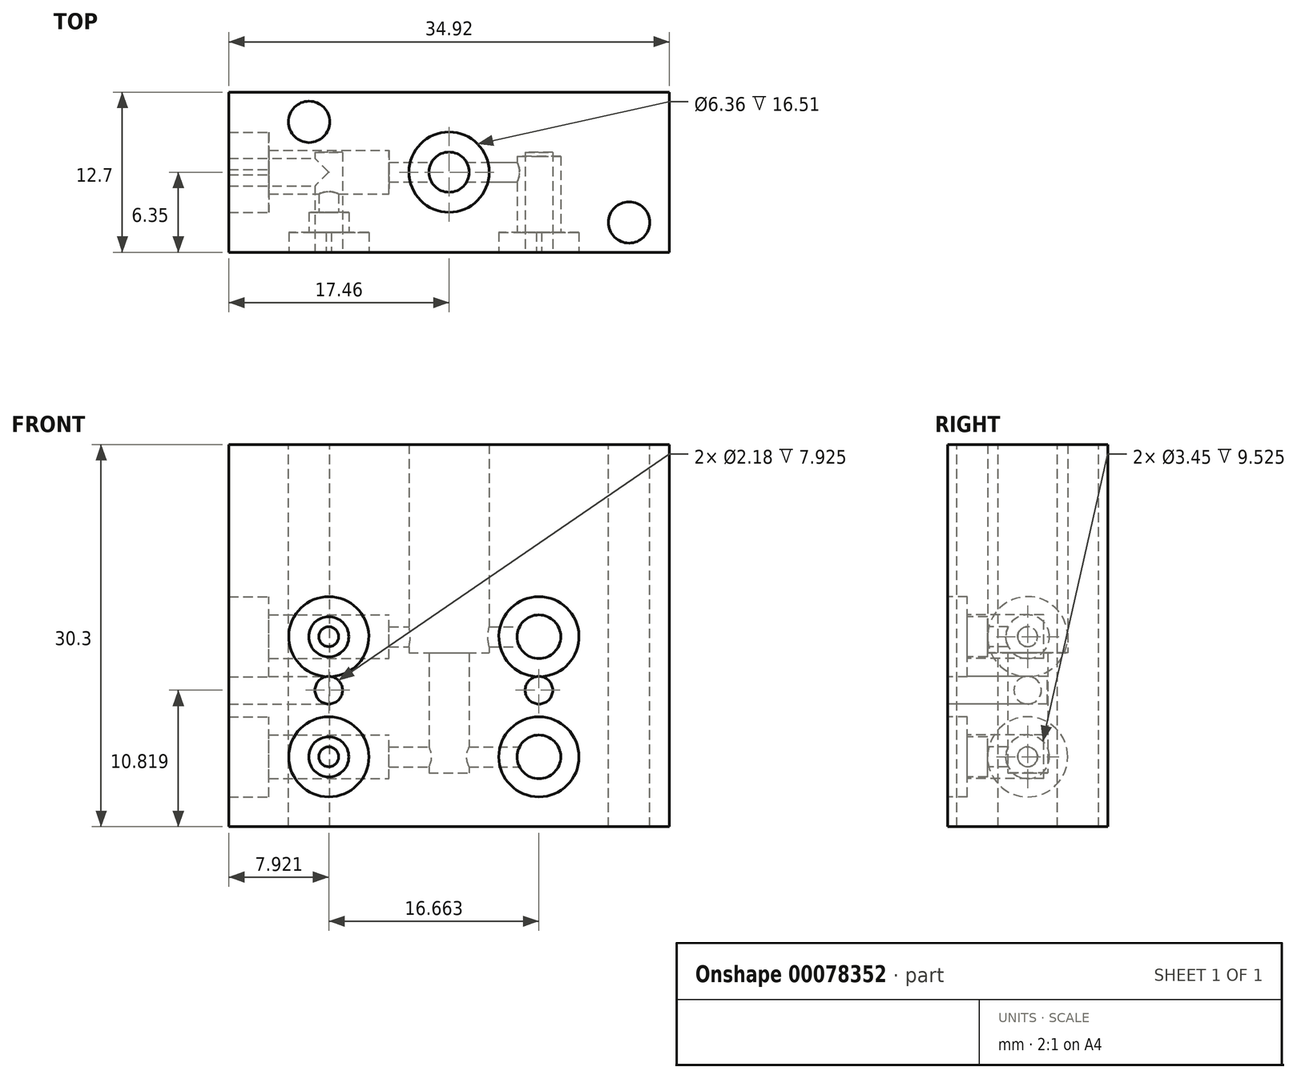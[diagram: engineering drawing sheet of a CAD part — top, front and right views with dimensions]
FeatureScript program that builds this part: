
annotation { "Feature Type Name" : "Feature", "Feature Type Description" : "" }
export const myFeature = defineFeature(function(context is Context, id is Id, definition is map)
    precondition{}
    {
        {
            var Q0;
            Q0=qCreatedBy(makeId("Front.planeOp"),FACE);
            var sketch = newSketch(context, id + "F0", { "sketchPlane" : qUnion([Q0])});
            skLineSegment(sketch, "E0.top", {"start": v(0, 15.15) * mm, "end": v(-17.46, 15.15) * mm});
            skLineSegment(sketch, "E0.right", {"start": v(-17.46, 0) * mm, "end": v(-17.46, 15.15) * mm});
            skLineSegment(sketch, "E1.MirrorCS", {"start": v(0, -15.15) * mm, "end": v(-17.46, -15.15) * mm});
            skLineSegment(sketch, "E2.MirrorCS", {"start": v(-17.46, 0) * mm, "end": v(-17.46, -15.15) * mm});
            skLineSegment(sketch, "E3.MirrorCS", {"start": v(0, 15.15) * mm, "end": v(17.46, 15.15) * mm});
            skLineSegment(sketch, "E4.MirrorCS", {"start": v(17.46, 0) * mm, "end": v(17.46, 15.15) * mm});
            skLineSegment(sketch, "E5.MirrorCS", {"start": v(17.46, 0) * mm, "end": v(17.46, -15.15) * mm});
            skLineSegment(sketch, "E6.MirrorCS", {"start": v(0, -15.15) * mm, "end": v(17.46, -15.15) * mm});
            skSolve(sketch);
        }
        {
            var Q0;
            Q0 = qSketchRegion(id + "F0", true);
            extrude(context, id + "F1", {"entities" : qUnion([Q0]), "endBound" : BoundingType.SYMMETRIC, "depth" : 12.7 * mm});
        }
        {
            var Q0;
            Q0=qCreatedBy(makeId("Front.planeOp"),FACE);
            var sketch = newSketch(context, id + "F2", { "sketchPlane" : qUnion([Q0])});
            skLineSegment(sketch, "E7", {"start": v(0, 0) * mm, "end": v(-17.46, 0) * mm, "construction": true});
            skLineSegment(sketch, "E8", {"start": v(-17.46, -3.26) * mm, "end": v(-14.29, -3.26) * mm});
            skLineSegment(sketch, "E9", {"start": v(-17.46, -0.09) * mm, "end": v(7.12, -0.09) * mm});
            skLineSegment(sketch, "E10", {"start": v(-14.29, -3.26) * mm, "end": v(-14.29, -1.82) * mm});
            skLineSegment(sketch, "E11", {"start": v(-4.76, -0.88) * mm, "end": v(-4.76, -1.82) * mm});
            skLineSegment(sketch, "E12", {"start": v(-4.76, -1.82) * mm, "end": v(-14.29, -1.82) * mm});
            skLineSegment(sketch, "E13", {"start": v(7.12, -0.09) * mm, "end": v(7.12, -0.88) * mm});
            skLineSegment(sketch, "E14", {"start": v(6.77, -0.88) * mm, "end": v(-4.76, -0.88) * mm});
            skPoint(sketch, "E14.endSnap0", {"position": v(-4.76, -0.95) * mm});
            skPoint(sketch, "E15.orphan", {"position": v(-4.76, -0.09) * mm});
            skLineSegment(sketch, "E16", {"start": v(-17.46, -0.09) * mm, "end": v(-17.46, -3.26) * mm});
            skArc(sketch, "E17", {"start": v(6.77, -0.88) * mm, "mid": v(7.6, -0.81) * mm, "end": v(7.99, -0.09) * mm});
            skLineSegment(sketch, "E18", {"start": v(7.12, -0.09) * mm, "end": v(7.99, -0.09) * mm});
            skSolve(sketch);
        }
        {
            var Q0;
            Q0 = qSketchRegion(id + "F2", true);
            var Q1;
            Q1=sQuery(id+"F2.wireOp",EDGE,"E9");
            revolve(context, id + "F3", {"operationType" : NewBodyOperationType.REMOVE, "entities" : qUnion([Q0]), "axis" : qUnion([Q1]), "revolveType" : RevolveType.FULL, "oppositeDirection" : true});
        }
        {
            var Q0;
            Q0=qCreatedBy(makeId("Front.planeOp"),FACE);
            var sketch = newSketch(context, id + "F4", { "sketchPlane" : qUnion([Q0])});
            skLineSegment(sketch, "E19", {"start": v(0, 0) * mm, "end": v(-17.46, 0) * mm, "construction": true});
            skLineSegment(sketch, "E20", {"start": v(-17.46, 0) * mm, "end": v(-17.46, -9.61) * mm, "construction": true});
            skLineSegment(sketch, "E21", {"start": v(-17.46, -9.61) * mm, "end": v(7.12, -9.61) * mm});
            skLineSegment(sketch, "E22", {"start": v(7.12, -9.61) * mm, "end": v(7.12, -10.4) * mm});
            skLineSegment(sketch, "E23", {"start": v(6.77, -10.4) * mm, "end": v(-4.76, -10.4) * mm});
            skPoint(sketch, "E24.endSnap0", {"position": v(-5.17, -9.61) * mm});
            skLineSegment(sketch, "E25", {"start": v(-4.76, -10.4) * mm, "end": v(-4.76, -11.34) * mm});
            skLineSegment(sketch, "E26", {"start": v(-17.46, -9.61) * mm, "end": v(-17.46, -12.79) * mm});
            skLineSegment(sketch, "E27", {"start": v(-17.46, -12.79) * mm, "end": v(-14.29, -12.79) * mm});
            skLineSegment(sketch, "E28", {"start": v(-14.29, -12.79) * mm, "end": v(-14.29, -11.34) * mm});
            skLineSegment(sketch, "E29", {"start": v(-14.29, -11.34) * mm, "end": v(-4.76, -11.34) * mm});
            skPoint(sketch, "E24.end.orphan", {"position": v(-4.76, -9.61) * mm});
            skArc(sketch, "E30", {"start": v(6.77, -10.4) * mm, "mid": v(7.6, -10.34) * mm, "end": v(7.99, -9.61) * mm});
            skLineSegment(sketch, "E31", {"start": v(7.12, -9.61) * mm, "end": v(7.99, -9.61) * mm});
            skSolve(sketch);
        }
        {
            var Q0;
            Q0 = qSketchRegion(id + "F4", true);
            var Q1;
            Q1=sQuery(id+"F4.wireOp",EDGE,"E21");
            revolve(context, id + "F5", {"operationType" : NewBodyOperationType.REMOVE, "entities" : qUnion([Q0]), "axis" : qUnion([Q1]), "revolveType" : RevolveType.FULL, "oppositeDirection" : true});
        }
        {
            var Q0;
            Q0=qCreatedBy(makeId("Front.planeOp"),FACE);
            var sketch = newSketch(context, id + "F6", { "sketchPlane" : qUnion([Q0])});
            skLineSegment(sketch, "E32", {"start": v(0, 0) * mm, "end": v(-17.46, 0) * mm, "construction": true});
            skLineSegment(sketch, "E33", {"start": v(-17.46, 0) * mm, "end": v(-17.46, -4.33) * mm, "construction": true});
            skLineSegment(sketch, "E34", {"start": v(-17.46, -4.33) * mm, "end": v(-9.54, -4.33) * mm});
            skLineSegment(sketch, "E35", {"start": v(-17.46, -4.33) * mm, "end": v(-17.46, -5.42) * mm});
            skLineSegment(sketch, "E36", {"start": v(-17.46, -5.42) * mm, "end": v(-9.54, -5.42) * mm});
            skArc(sketch, "E37", {"start": v(-9.54, -5.42) * mm, "mid": v(-8.77, -5.1) * mm, "end": v(-8.45, -4.33) * mm});
            skLineSegment(sketch, "E38", {"start": v(-9.54, -4.33) * mm, "end": v(-8.45, -4.33) * mm});
            skSolve(sketch);
        }
        {
            var Q0;
            Q0 = qSketchRegion(id + "F6", true);
            var Q1;
            Q1=sQuery(id+"F6.wireOp",EDGE,"E34");
            revolve(context, id + "F7", {"operationType" : NewBodyOperationType.REMOVE, "entities" : qUnion([Q0]), "axis" : qUnion([Q1]), "revolveType" : RevolveType.FULL, "oppositeDirection" : true});
        }
        {
            var Q0;
            Q0=qCreatedBy(makeId("Front.planeOp"),FACE);
            var sketch = newSketch(context, id + "F8", { "sketchPlane" : qUnion([Q0])});
            skLineSegment(sketch, "E39", {"start": v(0, 0) * mm, "end": v(0, 15.15) * mm, "construction": true});
            skLineSegment(sketch, "E40", {"start": v(0, 15.15) * mm, "end": v(3.18, 15.15) * mm});
            skLineSegment(sketch, "E41", {"start": v(3.18, 15.15) * mm, "end": v(3.18, -1.36) * mm});
            skLineSegment(sketch, "E42", {"start": v(0, 15.15) * mm, "end": v(0, -10.88) * mm});
            skLineSegment(sketch, "E43", {"start": v(0, -10.88) * mm, "end": v(1.6, -10.88) * mm});
            skLineSegment(sketch, "E44", {"start": v(1.6, -10.88) * mm, "end": v(1.6, -1.36) * mm});
            skLineSegment(sketch, "E45", {"start": v(1.6, -1.36) * mm, "end": v(3.18, -1.36) * mm});
            skSolve(sketch);
        }
        {
            var Q0;
            Q0 = qSketchRegion(id + "F8", true);
            var Q1;
            Q1=sQuery(id+"F8.wireOp",EDGE,"E42");
            revolve(context, id + "F9", {"operationType" : NewBodyOperationType.REMOVE, "entities" : qUnion([Q0]), "axis" : qUnion([Q1]), "revolveType" : RevolveType.FULL, "oppositeDirection" : true});
        }
        {
            var Q0;
            Q0=makeQuery(id+"F1.opExtrude","SWEPT_FACE",FACE,{"disambiguationData":[OSD([sQuery(id+"F0.wireOp",EDGE,"E0.top"),sQuery(id+"F0.wireOp",EDGE,"E3.MirrorCS")])]});
            var sketch = newSketch(context, id + "F10", { "sketchPlane" : qUnion([Q0])});
            skLineSegment(sketch, "E46", {"start": v(0, 0) * mm, "end": v(14.27, 0) * mm, "construction": true});
            skLineSegment(sketch, "E47", {"start": v(14.27, 0) * mm, "end": v(14.27, -3.99) * mm, "construction": true});
            skCircle(sketch, "E48", {"center": v(14.27, -3.99) * mm, "radius": 1.64 * mm});
            skLineSegment(sketch, "E49", {"start": v(0, 0) * mm, "end": v(-11.1, 0) * mm, "construction": true});
            skLineSegment(sketch, "E50", {"start": v(-11.1, 0) * mm, "end": v(-11.1, 3.99) * mm, "construction": true});
            skCircle(sketch, "E51", {"center": v(-11.1, 3.99) * mm, "radius": 1.64 * mm});
            skSolve(sketch);
        }
        {
            var Q0;
            Q0 = qSketchRegion(id + "F10", true);
            extrude(context, id + "F11", {"entities" : qUnion([Q0]), "operationType" : NewBodyOperationType.REMOVE, "oppositeDirection" : true, "depth" : 50.8 * mm});
        }
        {
            var Q0;
            Q0=makeQuery(id+"F1.opExtrude","CAP_FACE",FACE,{"disambiguationData":[OSD([sQuery(id+"F0.wireOp",EDGE,"E0.top"),sQuery(id+"F0.wireOp",EDGE,"E0.right"),sQuery(id+"F0.wireOp",EDGE,"E1.MirrorCS"),sQuery(id+"F0.wireOp",EDGE,"E2.MirrorCS"),sQuery(id+"F0.wireOp",EDGE,"E3.MirrorCS"),sQuery(id+"F0.wireOp",EDGE,"E4.MirrorCS"),sQuery(id+"F0.wireOp",EDGE,"E5.MirrorCS"),sQuery(id+"F0.wireOp",EDGE,"E6.MirrorCS")])],"isStart":false});
            var sketch = newSketch(context, id + "F12", { "sketchPlane" : qUnion([Q0])});
            skLineSegment(sketch, "E52", {"start": v(0, 0) * mm, "end": v(7.12, 0) * mm, "construction": true});
            skPoint(sketch, "E52.endSnap0", {"position": v(17.46, 0) * mm});
            skLineSegment(sketch, "E53", {"start": v(7.12, 0) * mm, "end": v(7.12, -0.09) * mm, "construction": true});
            skCircle(sketch, "E54", {"center": v(7.12, -0.09) * mm, "radius": 3.18 * mm});
            skLineSegment(sketch, "E55", {"start": v(7.12, 0) * mm, "end": v(7.12, -9.61) * mm, "construction": true});
            skCircle(sketch, "E56", {"center": v(7.12, -9.61) * mm, "radius": 3.18 * mm});
            skSolve(sketch);
        }
        {
            var Q0;
            Q0=makeQuery(id+"F12.imprint","IMPRINT",FACE,{"disambiguationData":[TD([[makeQuery(id+"F12.imprint","IMPRINT",EDGE,{"derivedFrom":sQuery(id+"F12.wireOp",EDGE,"E54")}),1.0]])]});
            var Q1;
            Q1=makeQuery(id+"F12.imprint","IMPRINT",FACE,{"disambiguationData":[TD([[makeQuery(id+"F12.imprint","IMPRINT",EDGE,{"derivedFrom":sQuery(id+"F12.wireOp",EDGE,"E56")}),1.0]])]});
            extrude(context, id + "F13", {"entities" : qUnion([Q0, Q1]), "operationType" : NewBodyOperationType.REMOVE, "oppositeDirection" : true, "depth" : 1.57 * mm});
        }
        {
            var Q0;
            Q0=makeQuery(id+"F1.opExtrude","CAP_FACE",FACE,{"disambiguationData":[OSD([sQuery(id+"F0.wireOp",EDGE,"E0.top"),sQuery(id+"F0.wireOp",EDGE,"E0.right"),sQuery(id+"F0.wireOp",EDGE,"E1.MirrorCS"),sQuery(id+"F0.wireOp",EDGE,"E2.MirrorCS"),sQuery(id+"F0.wireOp",EDGE,"E3.MirrorCS"),sQuery(id+"F0.wireOp",EDGE,"E4.MirrorCS"),sQuery(id+"F0.wireOp",EDGE,"E5.MirrorCS"),sQuery(id+"F0.wireOp",EDGE,"E6.MirrorCS")])],"isStart":false});
            var sketch = newSketch(context, id + "F14", { "sketchPlane" : qUnion([Q0])});
            skCircle(sketch, "E57", {"center": v(7.12, -0.09) * mm, "radius": 1.73 * mm});
            skCircle(sketch, "E58", {"center": v(7.12, -9.61) * mm, "radius": 1.73 * mm});
            skSolve(sketch);
        }
        {
            var Q0;
            Q0 = qSketchRegion(id + "F14", true);
            extrude(context, id + "F15", {"entities" : qUnion([Q0]), "operationType" : NewBodyOperationType.REMOVE, "oppositeDirection" : true, "depth" : 7.62 * mm});
        }
        {
            var Q0;
            Q0=makeQuery(id+"F1.opExtrude","CAP_FACE",FACE,{"disambiguationData":[OSD([sQuery(id+"F0.wireOp",EDGE,"E0.top"),sQuery(id+"F0.wireOp",EDGE,"E0.right"),sQuery(id+"F0.wireOp",EDGE,"E1.MirrorCS"),sQuery(id+"F0.wireOp",EDGE,"E2.MirrorCS"),sQuery(id+"F0.wireOp",EDGE,"E3.MirrorCS"),sQuery(id+"F0.wireOp",EDGE,"E4.MirrorCS"),sQuery(id+"F0.wireOp",EDGE,"E5.MirrorCS"),sQuery(id+"F0.wireOp",EDGE,"E6.MirrorCS")])],"isStart":false});
            var sketch = newSketch(context, id + "F16", { "sketchPlane" : qUnion([Q0])});
            skLineSegment(sketch, "E59", {"start": v(0, 0) * mm, "end": v(-9.54, 0) * mm, "construction": true});
            skLineSegment(sketch, "E60", {"start": v(-9.54, 0) * mm, "end": v(-9.54, -0.09) * mm, "construction": true});
            skLineSegment(sketch, "E61", {"start": v(-9.54, 0) * mm, "end": v(-9.54, -9.61) * mm, "construction": true});
            skCircle(sketch, "E62", {"center": v(-9.54, -0.09) * mm, "radius": 3.18 * mm});
            skCircle(sketch, "E63", {"center": v(-9.54, -9.61) * mm, "radius": 3.18 * mm});
            skSolve(sketch);
        }
        {
            var Q0;
            Q0 = qSketchRegion(id + "F16", true);
            extrude(context, id + "F17", {"entities" : qUnion([Q0]), "operationType" : NewBodyOperationType.REMOVE, "oppositeDirection" : true, "depth" : 1.57 * mm});
        }
        {
            var Q0;
            Q0=makeQuery(id+"F1.opExtrude","CAP_FACE",FACE,{"disambiguationData":[OSD([sQuery(id+"F0.wireOp",EDGE,"E0.top"),sQuery(id+"F0.wireOp",EDGE,"E0.right"),sQuery(id+"F0.wireOp",EDGE,"E1.MirrorCS"),sQuery(id+"F0.wireOp",EDGE,"E2.MirrorCS"),sQuery(id+"F0.wireOp",EDGE,"E3.MirrorCS"),sQuery(id+"F0.wireOp",EDGE,"E4.MirrorCS"),sQuery(id+"F0.wireOp",EDGE,"E5.MirrorCS"),sQuery(id+"F0.wireOp",EDGE,"E6.MirrorCS")])],"isStart":false});
            var sketch = newSketch(context, id + "F18", { "sketchPlane" : qUnion([Q0])});
            skCircle(sketch, "E64", {"center": v(-9.54, -0.09) * mm, "radius": 1.59 * mm});
            skCircle(sketch, "E65", {"center": v(-9.54, -9.61) * mm, "radius": 1.59 * mm});
            skSolve(sketch);
        }
        {
            var Q0;
            Q0 = qSketchRegion(id + "F18", true);
            extrude(context, id + "F19", {"entities" : qUnion([Q0]), "operationType" : NewBodyOperationType.REMOVE, "oppositeDirection" : true, "depth" : 3.17 * mm});
        }
        {
            var Q0;
            Q0=makeQuery(id+"F1.opExtrude","CAP_FACE",FACE,{"disambiguationData":[OSD([sQuery(id+"F0.wireOp",EDGE,"E0.top"),sQuery(id+"F0.wireOp",EDGE,"E0.right"),sQuery(id+"F0.wireOp",EDGE,"E1.MirrorCS"),sQuery(id+"F0.wireOp",EDGE,"E2.MirrorCS"),sQuery(id+"F0.wireOp",EDGE,"E3.MirrorCS"),sQuery(id+"F0.wireOp",EDGE,"E4.MirrorCS"),sQuery(id+"F0.wireOp",EDGE,"E5.MirrorCS"),sQuery(id+"F0.wireOp",EDGE,"E6.MirrorCS")])],"isStart":false});
            var sketch = newSketch(context, id + "F20", { "sketchPlane" : qUnion([Q0])});
            skCircle(sketch, "E66", {"center": v(-9.54, -0.09) * mm, "radius": 0.79 * mm});
            skCircle(sketch, "E67", {"center": v(-9.54, -9.61) * mm, "radius": 0.79 * mm});
            skSolve(sketch);
        }
        {
            var Q0;
            Q0 = qSketchRegion(id + "F20", true);
            extrude(context, id + "F21", {"entities" : qUnion([Q0]), "operationType" : NewBodyOperationType.REMOVE, "oppositeDirection" : true, "depth" : 6.35 * mm});
        }
        {
            var Q0;
            Q0=makeQuery(id+"F1.opExtrude","CAP_FACE",FACE,{"disambiguationData":[OSD([sQuery(id+"F0.wireOp",EDGE,"E0.top"),sQuery(id+"F0.wireOp",EDGE,"E0.right"),sQuery(id+"F0.wireOp",EDGE,"E1.MirrorCS"),sQuery(id+"F0.wireOp",EDGE,"E2.MirrorCS"),sQuery(id+"F0.wireOp",EDGE,"E3.MirrorCS"),sQuery(id+"F0.wireOp",EDGE,"E4.MirrorCS"),sQuery(id+"F0.wireOp",EDGE,"E5.MirrorCS"),sQuery(id+"F0.wireOp",EDGE,"E6.MirrorCS")])],"isStart":false});
            var sketch = newSketch(context, id + "F22", { "sketchPlane" : qUnion([Q0])});
            skLineSegment(sketch, "E68", {"start": v(7.12, 0) * mm, "end": v(7.12, -4.33) * mm, "construction": true});
            skLineSegment(sketch, "E69", {"start": v(0, 0) * mm, "end": v(7.12, 0) * mm, "construction": true});
            skLineSegment(sketch, "E70", {"start": v(-9.54, 0) * mm, "end": v(0, 0) * mm, "construction": true});
            skLineSegment(sketch, "E71", {"start": v(-9.54, 0) * mm, "end": v(-9.54, -4.33) * mm, "construction": true});
            skCircle(sketch, "E72", {"center": v(-9.54, -4.33) * mm, "radius": 1.1 * mm});
            skCircle(sketch, "E73", {"center": v(7.12, -4.33) * mm, "radius": 1.1 * mm});
            skSolve(sketch);
        }
        {
            var Q0;
            Q0 = qSketchRegion(id + "F22", true);
            extrude(context, id + "F23", {"entities" : qUnion([Q0]), "operationType" : NewBodyOperationType.REMOVE, "oppositeDirection" : true, "depth" : 7.92 * mm});
        }
    });
